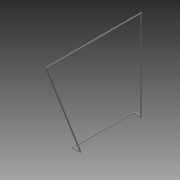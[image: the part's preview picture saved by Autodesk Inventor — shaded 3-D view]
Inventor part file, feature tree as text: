
AUTODESK INVENTOR PART (.ipt)
format: ipt  version: 2013 (Build 170138000, 138)  size: 143,360 bytes
history: native  units: in
note: dims shown in document units (in); Inventor stores cm internally (conversion verified against a paired STEP export)
features: extrude x5, sketch x5, fillet x1
ambient origin geometry x8: Origin, YZ Plane, XZ Plane, XY Plane, X Axis, Y Axis, Z Axis, Center Point
bodies: Solid1 (feature_tree)
feature tree (11):
  extrude  "Extrusion1"  Depth=15.0in
  extrude  "Extrusion2"  Depth=0.25in
  extrude  "Extrusion3"  Depth=0.25in
  extrude  "Extrusion4"  Depth=1.5in TaperAngle=0.0deg
  extrude  "Extrusion5"  Depth=22.0in
  fillet  "Fillet1"  Radius=0.25in
  sketch  "Sketch1"  dims[d0=0.25in d1=15.0in]
  sketch  "Sketch2"  dims[d2=0.25in d3=0.0in d4=0.25in]
  sketch  "Sketch3"  dims[d5=0.25in d6=0.25in]
  sketch  "Sketch4"  dims[d7=0.25in d8=1.5in d9=0.0in]
  sketch  "Sketch5"  dims[d10=0.25in d11=22.0in d12=0.25in d13=0.0in d14=23.25in d15=0.25in d16=0.25in d17=0.0in d18=21.75in d20=8.25in d22=0.25in d23=90.0deg d24=0.25in d25=0.25in d26=0.25in d27=0.0in d28=0.125in]
